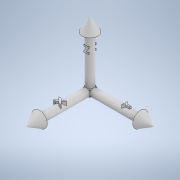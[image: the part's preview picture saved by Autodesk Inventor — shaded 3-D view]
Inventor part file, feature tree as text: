
AUTODESK INVENTOR PART (.ipt)
format: ipt  version: 2020 (Build 240168000, 168)  size: 362,496 bytes
history: native  units: in
note: dims shown in document units (in); Inventor stores cm internally (conversion verified against a paired STEP export)
features: extrude x10, sketch x10, fillet x5
ambient origin geometry x8: Origin, YZ Plane, XZ Plane, XY Plane, X Axis, Y Axis, Z Axis, Center Point
bodies: Solid1 (feature_tree)
feature tree (25):
  extrude  "Extrusion1"  Depth=0.5in TaperAngle=0.0deg
  extrude  "Extrusion2"  Depth=0.5in TaperAngle=0.0deg
  extrude  "Extrusion4"  Depth=0.5in
  extrude  "Extrusion5"  Depth=0.25in
  sketch  "Sketch6"  dims[d15=0.25in d16=0.5in]
  extrude  "Extrusion7"  Depth=0.5in
  extrude  "Extrusion8"  Depth=1.0in
  extrude  "Extrusion9"  Depth=1.0in
  extrude  "Extrusion10"  Depth=0.1in
  fillet  "Fillet4"  Radius=0.25in
  fillet  "Fillet5"  Radius=0.25in
  fillet  "Fillet10"  Radius=0.125in
  fillet  "Fillet11"  Radius=0.05in
  fillet  "Fillet12"  Radius=0.1in
  extrude  "Extrusion11"  Depth=0.1in
  extrude  "Extrusion12"  Depth=0.25in
  sketch  "Sketch1"  dims[d0=0.5in d1=3.5in d2=0.0in]
  sketch  "Sketch2"  dims[d3=0.5in d4=0.0in d7=3.0in d8=0.0in]
  sketch  "Sketch4"  dims[d9=3.0in d10=0.0in d12=0.5in]
  sketch  "Sketch5"  dims[d13=0.5in d14=0.25in]
  sketch  "Sketch8"  dims[d26=1.0in d27=1.0in d28=-0.2061in]
  sketch  "Sketch9"  dims[d29=1.0in d30=1.0in d31=-0.2061in]
  sketch  "Sketch10"  dims[d32=1.0in d33=1.0in d34=-0.2061in d38=0.25in d39=0.0in d40=0.25in d41=0.125in d45=0.05in d46=0.1in]
  sketch  "Sketch11"  dims[d47=0.1in d49=0.65in]
  sketch  "Sketch13"  dims[d50=180.0deg d52=0.25in d53=135.0deg d58=135.0deg d59=0.25in d60=0.0in d73=0.65in d74=0.15in d75=0.1in d76=0.1in d77=0.3in d78=0.5in d79=0.0in d80=0.5in d81=0.0344in d82=0.5in d83=0.0344in]
